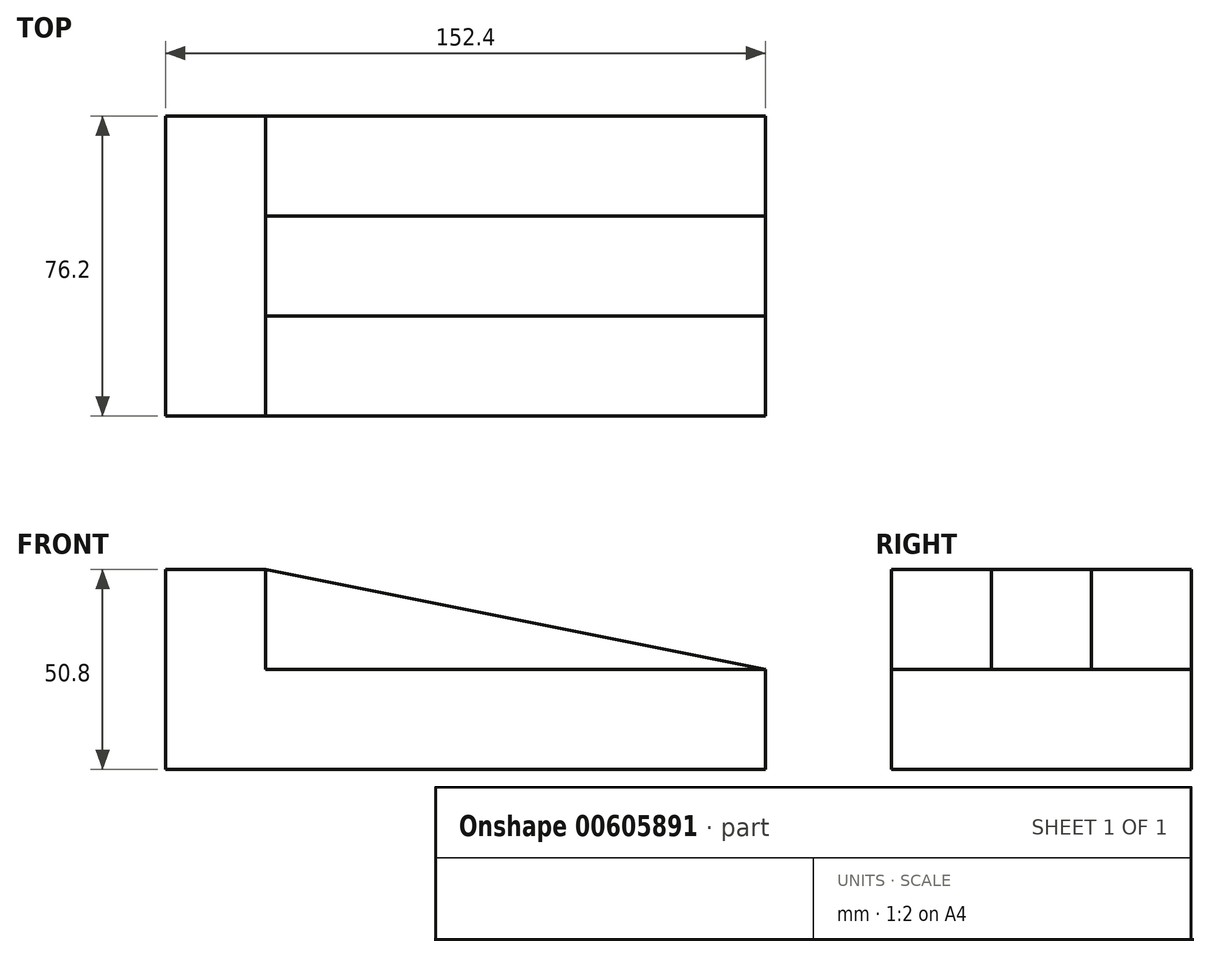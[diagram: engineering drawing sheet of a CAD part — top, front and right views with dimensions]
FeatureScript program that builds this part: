
annotation { "Feature Type Name" : "Feature", "Feature Type Description" : "" }
export const myFeature = defineFeature(function(context is Context, id is Id, definition is map)
    precondition{}
    {
        {
            var Q0;
            Q0=qCreatedBy(makeId("Front.planeOp"),FACE);
            var sketch = newSketch(context, id + "F0", { "sketchPlane" : qUnion([Q0])});
            skLineSegment(sketch, "E0", {"start": v(-136.53, 25.4) * mm, "end": v(-136.53, -25.4) * mm});
            skLineSegment(sketch, "E1", {"start": v(-136.53, -25.4) * mm, "end": v(15.87, -25.4) * mm});
            skLineSegment(sketch, "E2", {"start": v(15.87, -25.4) * mm, "end": v(15.87, 0) * mm});
            skLineSegment(sketch, "E3", {"start": v(-136.53, 25.4) * mm, "end": v(-111.13, 25.4) * mm});
            skLineSegment(sketch, "E4", {"start": v(-111.13, 25.4) * mm, "end": v(15.87, 0) * mm});
            skSolve(sketch);
        }
        {
            var Q0;
            Q0=makeQuery(id+"F0.imprint","IMPRINT",FACE,{"disambiguationData":[TD([[makeQuery(id+"F0.imprint","IMPRINT",EDGE,{"derivedFrom":sQuery(id+"F0.wireOp",EDGE,"E0")}),1.0]])]});
            extrude(context, id + "F1", {"entities" : qUnion([Q0]), "depth" : 76.2 * mm, "offsetDistance" : 25.4 * mm});
        }
        {
            var Q0;
            Q0=makeQuery(id+"F1.opExtrude","SWEPT_FACE",FACE,{"disambiguationData":[OSD([sQuery(id+"F0.wireOp",EDGE,"E3")])]});
            var sketch = newSketch(context, id + "F2", { "sketchPlane" : qUnion([Q0])});
            skLineSegment(sketch, "E5.bottom", {"start": v(-111.13, 0) * mm, "end": v(15.87, 0) * mm});
            skLineSegment(sketch, "E5.top", {"start": v(-111.13, -25.4) * mm, "end": v(15.87, -25.4) * mm});
            skLineSegment(sketch, "E5.left", {"start": v(-111.13, 0) * mm, "end": v(-111.13, -25.4) * mm});
            skLineSegment(sketch, "E5.right", {"start": v(15.87, 0) * mm, "end": v(15.87, -25.4) * mm});
            skLineSegment(sketch, "E6.bottom", {"start": v(-111.13, -76.2) * mm, "end": v(15.87, -76.2) * mm});
            skLineSegment(sketch, "E6.top", {"start": v(-111.13, -50.8) * mm, "end": v(15.87, -50.8) * mm});
            skLineSegment(sketch, "E6.left", {"start": v(-111.13, -76.2) * mm, "end": v(-111.13, -50.8) * mm});
            skLineSegment(sketch, "E6.right", {"start": v(15.87, -76.2) * mm, "end": v(15.87, -50.8) * mm});
            skSolve(sketch);
        }
        {
            var Q0;
            Q0=makeQuery(id+"F2.imprint","IMPRINT",FACE,{"disambiguationData":[TD([[makeQuery(id+"F2.imprint","IMPRINT",EDGE,{"derivedFrom":sQuery(id+"F2.wireOp",EDGE,"E6.bottom")}),1.0]])]});
            var Q1;
            Q1=makeQuery(id+"F2.imprint","IMPRINT",FACE,{"disambiguationData":[TD([[makeQuery(id+"F2.imprint","IMPRINT",EDGE,{"derivedFrom":sQuery(id+"F2.wireOp",EDGE,"E5.bottom")}),-1.0]])]});
            extrude(context, id + "F3", {"entities" : qUnion([Q0, Q1]), "operationType" : NewBodyOperationType.REMOVE, "oppositeDirection" : true, "depth" : 25.4 * mm, "offsetDistance" : 25.4 * mm});
        }
    });
